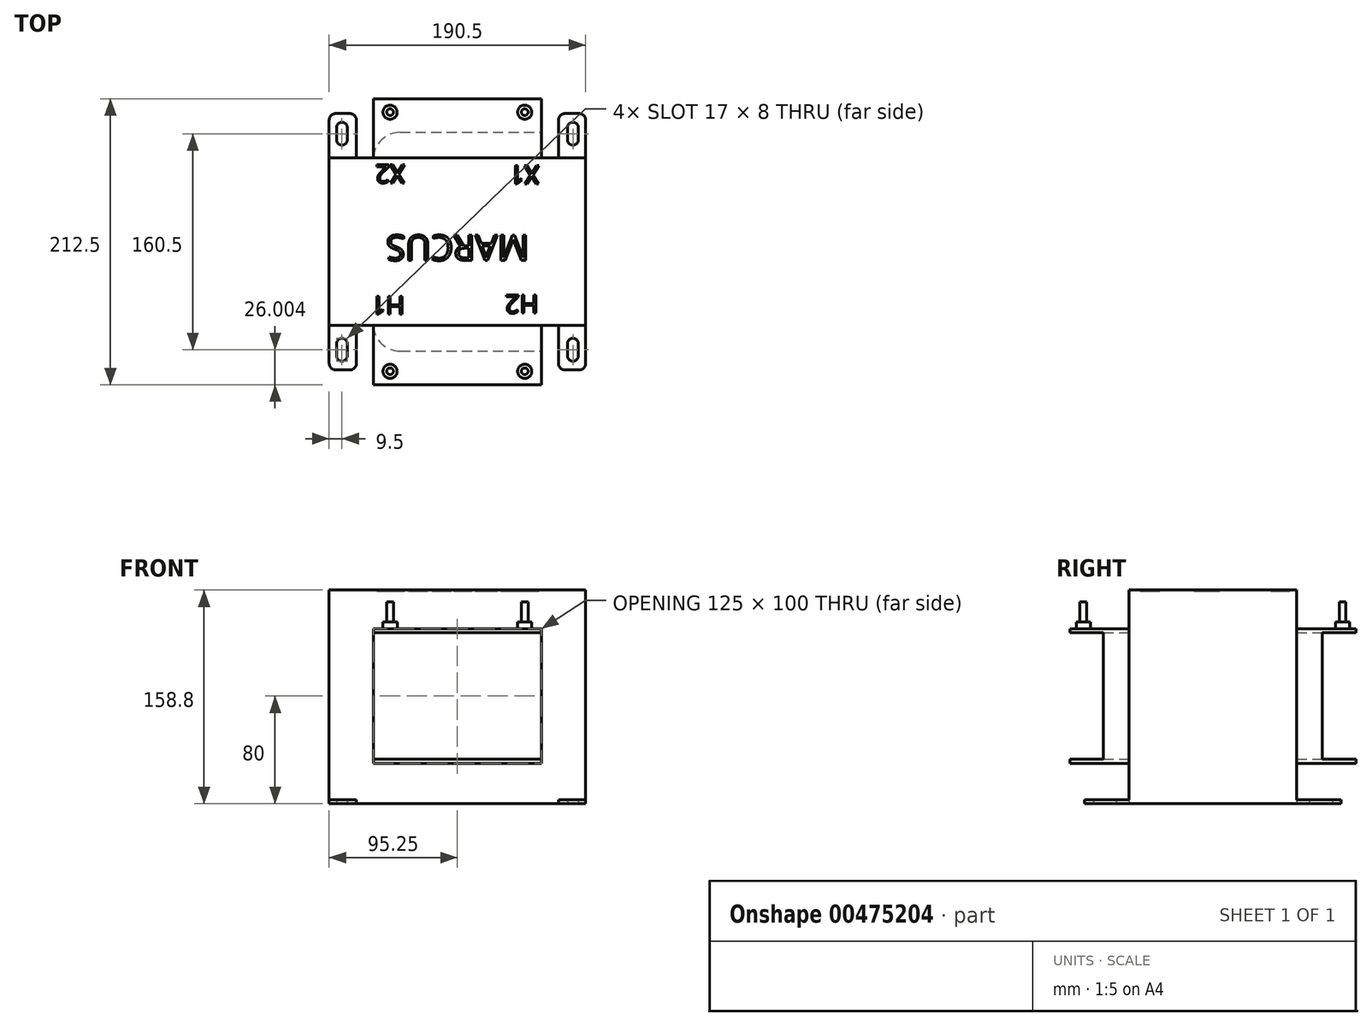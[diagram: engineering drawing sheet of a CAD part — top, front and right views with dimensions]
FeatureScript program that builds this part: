
annotation { "Feature Type Name" : "Feature", "Feature Type Description" : "" }
export const myFeature = defineFeature(function(context is Context, id is Id, definition is map)
    precondition{}
    {
        {
            var Q0;
            Q0=qCreatedBy(makeId("Top.planeOp"),FACE);
            var sketch = newSketch(context, id + "F0", { "sketchPlane" : qUnion([Q0])});
            skLineSegment(sketch, "E0.bottom", {"start": v(0, 1.31) * mm, "end": v(190.5, 1.31) * mm});
            skLineSegment(sketch, "E0.top", {"start": v(0, 191.81) * mm, "end": v(190.5, 191.81) * mm});
            skLineSegment(sketch, "E0.left", {"start": v(0, 1.31) * mm, "end": v(0, 191.81) * mm});
            skLineSegment(sketch, "E0.right", {"start": v(190.5, 1.31) * mm, "end": v(190.5, 191.81) * mm});
            skLineSegment(sketch, "E1.bottom", {"start": v(20.25, 1.31) * mm, "end": v(170.25, 1.31) * mm});
            skLineSegment(sketch, "E1.top", {"start": v(20.25, 34.31) * mm, "end": v(170.25, 34.31) * mm});
            skLineSegment(sketch, "E1.left", {"start": v(20.25, 1.31) * mm, "end": v(20.25, 34.31) * mm});
            skLineSegment(sketch, "E1.right", {"start": v(170.25, 1.31) * mm, "end": v(170.25, 34.31) * mm});
            skLineSegment(sketch, "E2.bottom", {"start": v(20.25, 191.81) * mm, "end": v(170.25, 191.81) * mm});
            skLineSegment(sketch, "E2.top", {"start": v(20.25, 158.81) * mm, "end": v(170.25, 158.81) * mm});
            skLineSegment(sketch, "E2.left", {"start": v(20.25, 191.81) * mm, "end": v(20.25, 158.81) * mm});
            skLineSegment(sketch, "E2.right", {"start": v(170.25, 191.81) * mm, "end": v(170.25, 158.81) * mm});
            skSolve(sketch);
        }
        {
            var Q0;
            {var subQ3=sQuery(id+"F0.wireOp",EDGE,"E0.left");Q0=makeQuery(id+"F0.imprint","IMPRINT",FACE,{"disambiguationData":[TD([[makeQuery(id+"F0.imprint","IMPRINT",EDGE,{"derivedFrom":subQ3}),-1.0]])]});}
            extrude(context, id + "F1", {"entities" : qUnion([Q0]), "depth" : 3 * mm});
        }
        {
            var Q0;
            Q0=makeQuery(id+"F1.opExtrude","CAP_FACE",FACE,{"disambiguationData":[OSD([sQuery(id+"F0.wireOp",EDGE,"E0.bottom"),sQuery(id+"F0.wireOp",EDGE,"E0.top"),sQuery(id+"F0.wireOp",EDGE,"E0.left"),sQuery(id+"F0.wireOp",EDGE,"E0.right"),sQuery(id+"F0.wireOp",EDGE,"E1.top"),sQuery(id+"F0.wireOp",EDGE,"E1.left"),sQuery(id+"F0.wireOp",EDGE,"E1.right"),sQuery(id+"F0.wireOp",EDGE,"E2.top"),sQuery(id+"F0.wireOp",EDGE,"E2.left"),sQuery(id+"F0.wireOp",EDGE,"E2.right")])],"isStart":false});
            var sketch = newSketch(context, id + "F2", { "sketchPlane" : qUnion([Q0])});
            skLineSegment(sketch, "E3.bottom", {"start": v(0, 158.81) * mm, "end": v(190.5, 158.81) * mm});
            skLineSegment(sketch, "E3.top", {"start": v(0, 34.31) * mm, "end": v(190.5, 34.31) * mm});
            skLineSegment(sketch, "E3.left", {"start": v(0, 158.81) * mm, "end": v(0, 34.31) * mm});
            skLineSegment(sketch, "E3.right", {"start": v(190.5, 158.81) * mm, "end": v(190.5, 34.31) * mm});
            skSolve(sketch);
        }
        {
            var Q0;
            Q0 = qSketchRegion(id + "F2", true);
            extrude(context, id + "F3", {"entities" : qUnion([Q0]), "operationType" : NewBodyOperationType.ADD, "depth" : 155.8 * mm});
        }
        {
            var Q0;
            Q0=makeQuery(id+"F3.boolean.opBoolean","MERGE",FACE,{"derivedFrom":[makeQuery(id+"F1.opExtrude","SWEPT_FACE",FACE,{"disambiguationData":[OSD([sQuery(id+"F0.wireOp",EDGE,"E2.top")])]}),makeQuery(id+"F3.opExtrude","SWEPT_FACE",FACE,{"disambiguationData":[OSD([sQuery(id+"F2.wireOp",EDGE,"E3.bottom")])]})]});
            var sketch = newSketch(context, id + "F4", { "sketchPlane" : qUnion([Q0])});
            skLineSegment(sketch, "E4.bottom", {"start": v(-32.75, 30) * mm, "end": v(-157.75, 30) * mm});
            skLineSegment(sketch, "E4.top", {"start": v(-32.75, 130) * mm, "end": v(-157.75, 130) * mm});
            skLineSegment(sketch, "E4.left", {"start": v(-32.75, 30) * mm, "end": v(-32.75, 130) * mm});
            skLineSegment(sketch, "E4.right", {"start": v(-157.75, 30) * mm, "end": v(-157.75, 130) * mm});
            skSolve(sketch);
        }
        {
            var Q0;
            Q0 = qSketchRegion(id + "F4", true);
            extrude(context, id + "F5", {"entities" : qUnion([Q0]), "operationType" : NewBodyOperationType.ADD, "depth" : 44 * mm});
        }
        {
            var Q0;
            Q0=makeQuery(id+"F3.boolean.opBoolean","MERGE",FACE,{"derivedFrom":[makeQuery(id+"F1.opExtrude","SWEPT_FACE",FACE,{"disambiguationData":[OSD([sQuery(id+"F0.wireOp",EDGE,"E1.top")])]}),makeQuery(id+"F3.opExtrude","SWEPT_FACE",FACE,{"disambiguationData":[OSD([sQuery(id+"F2.wireOp",EDGE,"E3.top")])]})]});
            var sketch = newSketch(context, id + "F6", { "sketchPlane" : qUnion([Q0])});
            skLineSegment(sketch, "E5.bottom", {"start": v(32.75, 130) * mm, "end": v(157.75, 130) * mm});
            skLineSegment(sketch, "E5.top", {"start": v(32.75, 30) * mm, "end": v(157.75, 30) * mm});
            skLineSegment(sketch, "E5.left", {"start": v(32.75, 130) * mm, "end": v(32.75, 30) * mm});
            skLineSegment(sketch, "E5.right", {"start": v(157.75, 130) * mm, "end": v(157.75, 30) * mm});
            skSolve(sketch);
        }
        {
            var Q0;
            Q0 = qSketchRegion(id + "F6", true);
            extrude(context, id + "F7", {"entities" : qUnion([Q0]), "operationType" : NewBodyOperationType.ADD, "depth" : 44 * mm});
        }
        {
            var Q0;
            Q0=makeQuery(id+"F1.opExtrude","CAP_FACE",FACE,{"disambiguationData":[OSD([sQuery(id+"F0.wireOp",EDGE,"E0.bottom"),sQuery(id+"F0.wireOp",EDGE,"E0.top"),sQuery(id+"F0.wireOp",EDGE,"E0.left"),sQuery(id+"F0.wireOp",EDGE,"E0.right"),sQuery(id+"F0.wireOp",EDGE,"E1.top"),sQuery(id+"F0.wireOp",EDGE,"E1.left"),sQuery(id+"F0.wireOp",EDGE,"E1.right"),sQuery(id+"F0.wireOp",EDGE,"E2.top"),sQuery(id+"F0.wireOp",EDGE,"E2.left"),sQuery(id+"F0.wireOp",EDGE,"E2.right")])],"isStart":true});
            var sketch = newSketch(context, id + "F8", { "sketchPlane" : qUnion([Q0])});
            skLineSegment(sketch, "E6", {"start": v(5.5, -181.31) * mm, "end": v(5.5, -172.31) * mm});
            skLineSegment(sketch, "E7", {"start": v(13.5, -172.31) * mm, "end": v(13.5, -181.31) * mm});
            skArc(sketch, "E8", {"start": v(13.5, -172.31) * mm, "mid": v(9.5, -168.31) * mm, "end": v(5.5, -172.31) * mm});
            skArc(sketch, "E9", {"start": v(5.5, -181.31) * mm, "mid": v(9.5, -185.31) * mm, "end": v(13.5, -181.31) * mm});
            skLineSegment(sketch, "E10", {"start": v(0, -96.56) * mm, "end": v(190.5, -96.56) * mm});
            skLineSegment(sketch, "E11", {"start": v(95.25, -158.81) * mm, "end": v(95.25, -34.31) * mm});
            skArc(sketch, "E12.MirrorCS", {"start": v(13.5, -20.81) * mm, "mid": v(9.5, -24.81) * mm, "end": v(5.5, -20.81) * mm});
            skLineSegment(sketch, "E13.MirrorCS", {"start": v(5.5, -11.81) * mm, "end": v(5.5, -20.81) * mm});
            skLineSegment(sketch, "E14.MirrorCS", {"start": v(13.5, -20.81) * mm, "end": v(13.5, -11.81) * mm});
            skArc(sketch, "E15.MirrorCS", {"start": v(5.5, -11.81) * mm, "mid": v(9.5, -7.81) * mm, "end": v(13.5, -11.81) * mm});
            skLineSegment(sketch, "E16.MirrorCS", {"start": v(95.25, -34.31) * mm, "end": v(95.25, -158.81) * mm});
            skLineSegment(sketch, "E17.MirrorCS", {"start": v(177, -20.81) * mm, "end": v(177, -11.81) * mm});
            skLineSegment(sketch, "E18.MirrorCS", {"start": v(185, -11.81) * mm, "end": v(185, -20.81) * mm});
            skArc(sketch, "E19.MirrorCS", {"start": v(185, -11.81) * mm, "mid": v(181, -7.81) * mm, "end": v(177, -11.81) * mm});
            skArc(sketch, "E20.MirrorCS", {"start": v(177, -20.81) * mm, "mid": v(181, -24.81) * mm, "end": v(185, -20.81) * mm});
            skLineSegment(sketch, "E21.MirrorCS", {"start": v(185, -181.31) * mm, "end": v(185, -172.31) * mm});
            skLineSegment(sketch, "E22.MirrorCS", {"start": v(177, -172.31) * mm, "end": v(177, -181.31) * mm});
            skArc(sketch, "E23.MirrorCS", {"start": v(177, -172.31) * mm, "mid": v(181, -168.31) * mm, "end": v(185, -172.31) * mm});
            skArc(sketch, "E24.MirrorCS", {"start": v(185, -181.31) * mm, "mid": v(181, -185.31) * mm, "end": v(177, -181.31) * mm});
            skSolve(sketch);
        }
        {
            var Q0;
            Q0 = qSketchRegion(id + "F8", true);
            extrude(context, id + "F9", {"entities" : qUnion([Q0]), "operationType" : NewBodyOperationType.REMOVE, "endBound" : BoundingType.THROUGH_ALL, "oppositeDirection" : true, "depth" : 25 * mm});
        }
        {
            var Q0;
            Q0=makeQuery(id+"F5.opExtrude","SWEPT_FACE",FACE,{"disambiguationData":[OSD([sQuery(id+"F4.wireOp",EDGE,"E4.top")])]});
            var sketch = newSketch(context, id + "F10", { "sketchPlane" : qUnion([Q0])});
            skCircle(sketch, "E25", {"center": v(145.25, 192.81) * mm, "radius": 5.25 * mm});
            skLineSegment(sketch, "E26", {"start": v(95.25, 202.81) * mm, "end": v(95.25, 158.81) * mm});
            skCircle(sketch, "E27.MirrorC", {"center": v(45.25, 192.81) * mm, "radius": 5.25 * mm});
            skSolve(sketch);
        }
        {
            var Q0;
            Q0 = qSketchRegion(id + "F10", true);
            extrude(context, id + "F11", {"entities" : qUnion([Q0]), "operationType" : NewBodyOperationType.ADD, "depth" : 5 * mm});
        }
        {
            var Q0;
            Q0=makeQuery(id+"F11.opExtrude","CAP_FACE",FACE,{"disambiguationData":[OSD([sQuery(id+"F10.wireOp",EDGE,"E25")])],"isStart":false});
            var sketch = newSketch(context, id + "F12", { "sketchPlane" : qUnion([Q0])});
            skCircle(sketch, "E28", {"center": v(145.25, 192.81) * mm, "radius": 2.5 * mm});
            skSolve(sketch);
        }
        {
            var Q0;
            Q0 = qSketchRegion(id + "F12", true);
            extrude(context, id + "F13", {"entities" : qUnion([Q0]), "operationType" : NewBodyOperationType.ADD, "depth" : 15 * mm});
        }
        {
            var Q0;
            Q0=makeQuery(id+"F11.opExtrude","CAP_FACE",FACE,{"disambiguationData":[OSD([sQuery(id+"F10.wireOp",EDGE,"E27.MirrorC")])],"isStart":false});
            var sketch = newSketch(context, id + "F14", { "sketchPlane" : qUnion([Q0])});
            skCircle(sketch, "E29", {"center": v(45.25, 192.81) * mm, "radius": 2.5 * mm});
            skSolve(sketch);
        }
        {
            var Q0;
            Q0 = qSketchRegion(id + "F14", true);
            extrude(context, id + "F15", {"entities" : qUnion([Q0]), "operationType" : NewBodyOperationType.ADD, "depth" : 15 * mm});
        }
        {
            var Q0;
            Q0=makeQuery(id+"F7.opExtrude","SWEPT_FACE",FACE,{"disambiguationData":[OSD([sQuery(id+"F6.wireOp",EDGE,"E5.bottom")])]});
            var sketch = newSketch(context, id + "F16", { "sketchPlane" : qUnion([Q0])});
            skCircle(sketch, "E30", {"center": v(45.25, 0.31) * mm, "radius": 5.25 * mm});
            skLineSegment(sketch, "E31", {"start": v(95.25, -9.69) * mm, "end": v(95.25, 34.31) * mm});
            skCircle(sketch, "E32.MirrorC", {"center": v(145.25, 0.31) * mm, "radius": 5.25 * mm});
            skSolve(sketch);
        }
        {
            var Q0;
            Q0 = qSketchRegion(id + "F16", true);
            extrude(context, id + "F17", {"entities" : qUnion([Q0]), "operationType" : NewBodyOperationType.ADD, "depth" : 5 * mm});
        }
        {
            var Q0;
            Q0=makeQuery(id+"F17.opExtrude","CAP_FACE",FACE,{"disambiguationData":[OSD([sQuery(id+"F16.wireOp",EDGE,"E30")])],"isStart":false});
            var sketch = newSketch(context, id + "F18", { "sketchPlane" : qUnion([Q0])});
            skCircle(sketch, "E33", {"center": v(45.25, 0.31) * mm, "radius": 2.5 * mm});
            skSolve(sketch);
        }
        {
            var Q0;
            Q0 = qSketchRegion(id + "F18", true);
            extrude(context, id + "F19", {"entities" : qUnion([Q0]), "operationType" : NewBodyOperationType.ADD, "depth" : 15 * mm});
        }
        {
            var Q0;
            Q0=makeQuery(id+"F17.opExtrude","CAP_FACE",FACE,{"disambiguationData":[OSD([sQuery(id+"F16.wireOp",EDGE,"E32.MirrorC")])],"isStart":false});
            var sketch = newSketch(context, id + "F20", { "sketchPlane" : qUnion([Q0])});
            skCircle(sketch, "E34", {"center": v(145.25, 0.31) * mm, "radius": 2.5 * mm});
            skSolve(sketch);
        }
        {
            var Q0;
            Q0 = qSketchRegion(id + "F20", true);
            extrude(context, id + "F21", {"entities" : qUnion([Q0]), "operationType" : NewBodyOperationType.ADD, "depth" : 15 * mm});
        }
        {
            var Q0;
            Q0=makeQuery(id+"F7.opExtrude","SWEPT_FACE",FACE,{"disambiguationData":[OSD([sQuery(id+"F6.wireOp",EDGE,"E5.right")])]});
            var sketch = newSketch(context, id + "F22", { "sketchPlane" : qUnion([Q0])});
            skLineSegment(sketch, "E35.bottom", {"start": v(-9.69, 127) * mm, "end": v(15.31, 127) * mm});
            skLineSegment(sketch, "E35.top", {"start": v(-9.69, 33) * mm, "end": v(15.31, 33) * mm});
            skLineSegment(sketch, "E35.left", {"start": v(-9.69, 127) * mm, "end": v(-9.69, 33) * mm});
            skLineSegment(sketch, "E35.right", {"start": v(15.31, 127) * mm, "end": v(15.31, 33) * mm});
            skSolve(sketch);
        }
        {
            var Q0;
            Q0 = qSketchRegion(id + "F22", true);
            extrude(context, id + "F23", {"entities" : qUnion([Q0]), "operationType" : NewBodyOperationType.REMOVE, "endBound" : BoundingType.THROUGH_ALL, "oppositeDirection" : true, "depth" : 25 * mm});
        }
        {
            var Q0;
            Q0=makeQuery(id+"F5.opExtrude","SWEPT_FACE",FACE,{"disambiguationData":[OSD([sQuery(id+"F4.wireOp",EDGE,"E4.right")])]});
            var sketch = newSketch(context, id + "F24", { "sketchPlane" : qUnion([Q0])});
            skLineSegment(sketch, "E36.bottom", {"start": v(177.81, 127) * mm, "end": v(202.81, 127) * mm});
            skLineSegment(sketch, "E36.top", {"start": v(177.81, 33) * mm, "end": v(202.81, 33) * mm});
            skLineSegment(sketch, "E36.left", {"start": v(177.81, 127) * mm, "end": v(177.81, 33) * mm});
            skLineSegment(sketch, "E36.right", {"start": v(202.81, 127) * mm, "end": v(202.81, 33) * mm});
            skSolve(sketch);
        }
        {
            var Q0;
            Q0 = qSketchRegion(id + "F24", true);
            extrude(context, id + "F25", {"entities" : qUnion([Q0]), "operationType" : NewBodyOperationType.REMOVE, "endBound" : BoundingType.THROUGH_ALL, "oppositeDirection" : true, "depth" : 25 * mm});
        }
        {
            var Q0;
            Q0=makeQuery(id+"F25.boolean.opBoolean","INTERSECT",EDGE,{"derivedFrom":[makeQuery(id+"F5.opExtrude","SWEPT_FACE",FACE,{"disambiguationData":[OSD([sQuery(id+"F4.wireOp",EDGE,"E4.left")])]}),makeQuery(id+"F25.opExtrude","SWEPT_FACE",FACE,{"disambiguationData":[OSD([sQuery(id+"F24.wireOp",EDGE,"E36.left")])]})]});
            fillet(context, id + "F26", {"entities" : qUnion([Q0]), "radius" : 20 * mm, "tangentPropagation" : true, "allowEdgeOverflow" : false});
        }
        {
            var Q0;
            Q0=makeQuery(id+"F25.boolean.opBoolean","COPY",EDGE,{"derivedFrom":makeQuery(id+"F25.opExtrude","CAP_EDGE",EDGE,{"disambiguationData":[OSD([sQuery(id+"F24.wireOp",EDGE,"E36.left")])],"isStart":true})});
            var Q1;
            Q1=makeQuery(id+"F23.boolean.opBoolean","INTERSECT",EDGE,{"derivedFrom":[makeQuery(id+"F7.opExtrude","SWEPT_FACE",FACE,{"disambiguationData":[OSD([sQuery(id+"F6.wireOp",EDGE,"E5.left")])]}),makeQuery(id+"F23.opExtrude","SWEPT_FACE",FACE,{"disambiguationData":[OSD([sQuery(id+"F22.wireOp",EDGE,"E35.right")])]})]});
            var Q2;
            Q2=makeQuery(id+"F23.boolean.opBoolean","COPY",EDGE,{"derivedFrom":makeQuery(id+"F23.opExtrude","CAP_EDGE",EDGE,{"disambiguationData":[OSD([sQuery(id+"F22.wireOp",EDGE,"E35.right")])],"isStart":true})});
            fillet(context, id + "F27", {"entities" : qUnion([Q0, Q1, Q2]), "radius" : 20 * mm, "tangentPropagation" : true, "allowEdgeOverflow" : false});
        }
        {
            var Q0;
            Q0=makeQuery(id+"F1.opExtrude","SWEPT_EDGE",EDGE,{"disambiguationData":[OSD([sQuery(id+"F0.wireOp",EDGE,"E0.bottom"),sQuery(id+"F0.wireOp",EDGE,"E0.left")])]});
            var Q1;
            Q1=makeQuery(id+"F1.opExtrude","SWEPT_EDGE",EDGE,{"disambiguationData":[OSD([sQuery(id+"F0.wireOp",EDGE,"E0.bottom"),sQuery(id+"F0.wireOp",EDGE,"E1.bottom"),sQuery(id+"F0.wireOp",EDGE,"E1.left")])]});
            var Q2;
            Q2=makeQuery(id+"F1.opExtrude","SWEPT_EDGE",EDGE,{"disambiguationData":[OSD([sQuery(id+"F0.wireOp",EDGE,"E0.bottom"),sQuery(id+"F0.wireOp",EDGE,"E1.bottom"),sQuery(id+"F0.wireOp",EDGE,"E1.right")])]});
            var Q3;
            Q3=makeQuery(id+"F1.opExtrude","SWEPT_EDGE",EDGE,{"disambiguationData":[OSD([sQuery(id+"F0.wireOp",EDGE,"E0.bottom"),sQuery(id+"F0.wireOp",EDGE,"E0.right")])]});
            var Q4;
            Q4=makeQuery(id+"F1.opExtrude","SWEPT_EDGE",EDGE,{"disambiguationData":[OSD([sQuery(id+"F0.wireOp",EDGE,"E0.top"),sQuery(id+"F0.wireOp",EDGE,"E0.right")])]});
            var Q5;
            Q5=makeQuery(id+"F1.opExtrude","SWEPT_EDGE",EDGE,{"disambiguationData":[OSD([sQuery(id+"F0.wireOp",EDGE,"E0.top"),sQuery(id+"F0.wireOp",EDGE,"E2.bottom"),sQuery(id+"F0.wireOp",EDGE,"E2.right")])]});
            var Q6;
            Q6=makeQuery(id+"F1.opExtrude","SWEPT_EDGE",EDGE,{"disambiguationData":[OSD([sQuery(id+"F0.wireOp",EDGE,"E0.top"),sQuery(id+"F0.wireOp",EDGE,"E2.bottom"),sQuery(id+"F0.wireOp",EDGE,"E2.left")])]});
            var Q7;
            Q7=makeQuery(id+"F1.opExtrude","SWEPT_EDGE",EDGE,{"disambiguationData":[OSD([sQuery(id+"F0.wireOp",EDGE,"E0.top"),sQuery(id+"F0.wireOp",EDGE,"E0.left")])]});
            fillet(context, id + "F28", {"entities" : qUnion([Q0, Q1, Q2, Q3, Q4, Q5, Q6, Q7]), "radius" : 5 * mm, "tangentPropagation" : true, "allowEdgeOverflow" : false});
        }
        {
            var Q0;
            Q0=makeQuery(id+"F3.opExtrude","CAP_FACE",FACE,{"disambiguationData":[OSD([sQuery(id+"F2.wireOp",EDGE,"E3.bottom"),sQuery(id+"F2.wireOp",EDGE,"E3.top"),sQuery(id+"F2.wireOp",EDGE,"E3.left"),sQuery(id+"F2.wireOp",EDGE,"E3.right")])],"isStart":false});
            var sketch = newSketch(context, id + "F29", { "sketchPlane" : qUnion([Q0])});
            skText(sketch, "E37", { "text": "MARCUS", "fontName": "OpenSans-Regular.ttf"});
            skText(sketch, "E38", { "text": "H1", "fontName": "OpenSans-Regular.ttf"});
            skText(sketch, "E39", { "text": "H2", "fontName": "OpenSans-Regular.ttf"});
            skText(sketch, "E40", { "text": "X1", "fontName": "OpenSans-Regular.ttf"});
            skText(sketch, "E41", { "text": "X2", "fontName": "OpenSans-Regular.ttf"});
            const initialGuessF29  = {"E37": [0.14857, 0.10137, -1, 0, 0.01884], "E38": [0.05596, 0.05607, -1, 0, 0.01363], "E39": [0.15535, 0.057, -1, 0, 0.01363], "E40": [0.15584, 0.1531, -1, 0, 0.01363], "E41": [0.05612, 0.15368, -1, 0, 0.01363]};
            skSetInitialGuess(sketch, initialGuessF29);
            skSolve(sketch);
        }
        {
            var Q0;
            Q0 = qSketchRegion(id + "F29", true);
            extrude(context, id + "F30", {"entities" : qUnion([Q0]), "operationType" : NewBodyOperationType.REMOVE, "oppositeDirection" : true, "depth" : 1 * mm});
        }
    });
